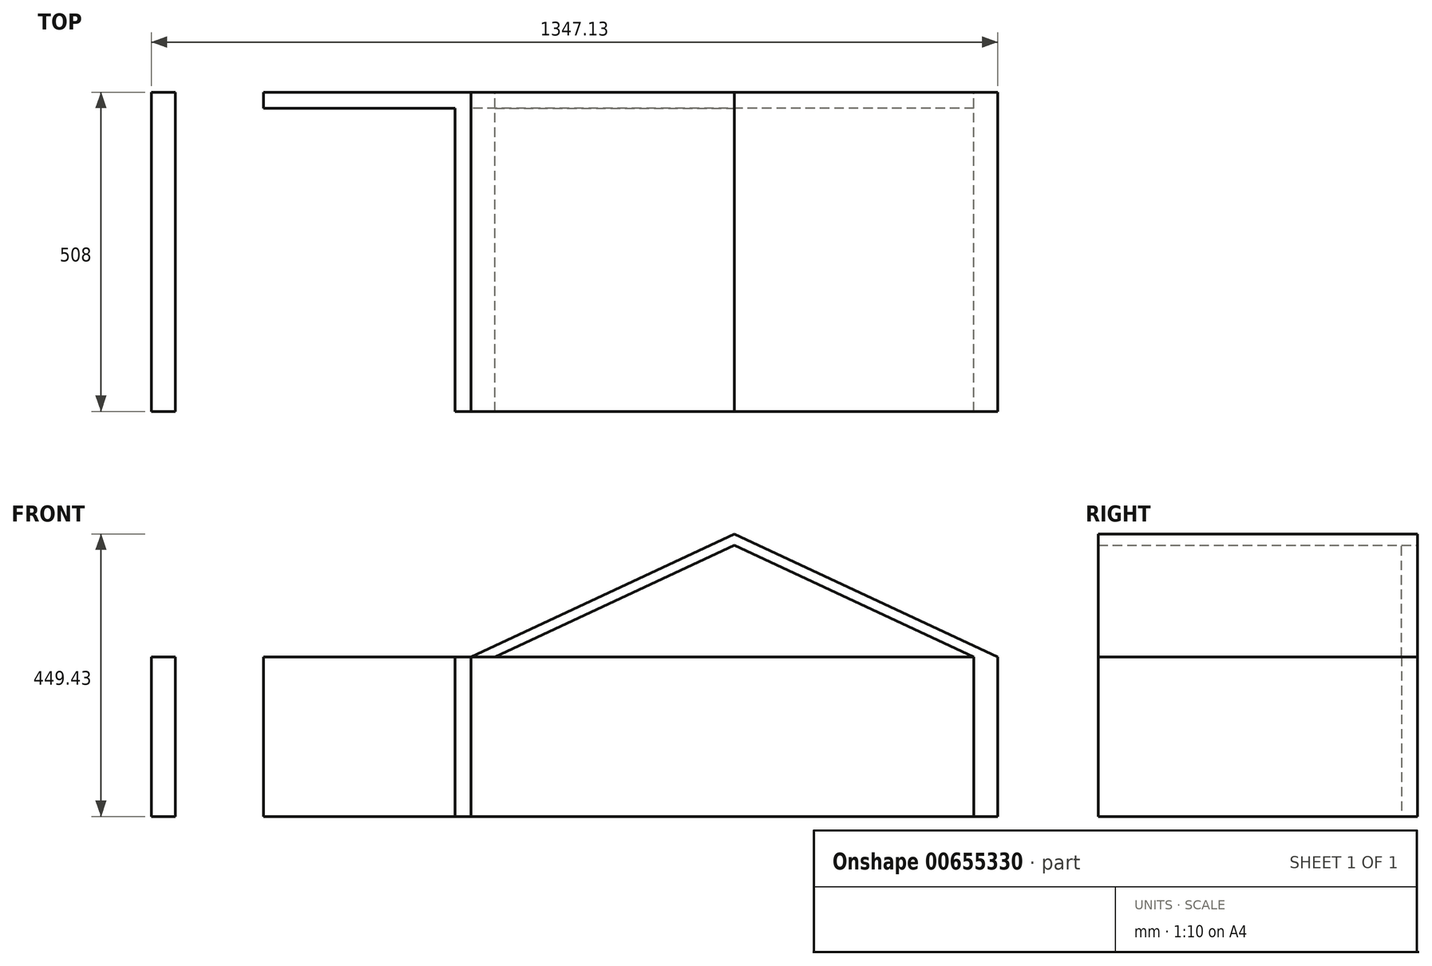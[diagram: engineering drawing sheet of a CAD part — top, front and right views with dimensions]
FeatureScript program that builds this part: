
annotation { "Feature Type Name" : "Feature", "Feature Type Description" : "" }
export const myFeature = defineFeature(function(context is Context, id is Id, definition is map)
    precondition{}
    {
        {
            var Q0;
            Q0=qCreatedBy(makeId("Front.planeOp"),FACE);
            var sketch = newSketch(context, id + "F0", { "sketchPlane" : qUnion([Q0])});
            skLineSegment(sketch, "E0", {"start": v(0, 117.3) * mm, "end": v(0, -136.7) * mm});
            skLineSegment(sketch, "E1", {"start": v(0, -136.7) * mm, "end": v(-25.4, -136.7) * mm});
            skLineSegment(sketch, "E2", {"start": v(-25.4, -136.7) * mm, "end": v(-25.4, 117.3) * mm});
            skLineSegment(sketch, "E3", {"start": v(-25.4, 117.3) * mm, "end": v(0, 117.3) * mm});
            skLineSegment(sketch, "E4", {"start": v(0, -136.7) * mm, "end": v(76.2, -136.7) * mm});
            skLineSegment(sketch, "E5", {"start": v(76.2, -136.7) * mm, "end": v(838.2, -136.7) * mm});
            skLineSegment(sketch, "E6", {"start": v(838.2, -136.7) * mm, "end": v(838.2, 117.3) * mm});
            skLineSegment(sketch, "E7", {"start": v(838.2, 117.3) * mm, "end": v(0, 117.3) * mm});
            skLineSegment(sketch, "E8", {"start": v(0, 117.3) * mm, "end": v(419.1, 312.72) * mm});
            skLineSegment(sketch, "E9", {"start": v(419.1, 312.72) * mm, "end": v(838.2, 117.3) * mm});
            skLineSegment(sketch, "E10", {"start": v(800.1, 117.3) * mm, "end": v(800.1, -136.7) * mm});
            skLineSegment(sketch, "E11", {"start": v(0, 117.3) * mm, "end": v(38.1, 117.3) * mm});
            skLineSegment(sketch, "E12", {"start": v(38.1, 117.3) * mm, "end": v(419.1, 294.95) * mm});
            skLineSegment(sketch, "E13", {"start": v(800.1, 117.3) * mm, "end": v(419.1, 294.95) * mm});
            skLineSegment(sketch, "E14", {"start": v(-470.83, 117.3) * mm, "end": v(-470.83, -136.7) * mm});
            skLineSegment(sketch, "E15", {"start": v(-470.83, 117.3) * mm, "end": v(-508.93, 117.3) * mm});
            skLineSegment(sketch, "E16", {"start": v(-508.93, 117.3) * mm, "end": v(-508.93, -136.7) * mm});
            skLineSegment(sketch, "E17", {"start": v(-508.93, -136.7) * mm, "end": v(-470.83, -136.7) * mm});
            skLineSegment(sketch, "E18", {"start": v(-330.2, 117.3) * mm, "end": v(-330.2, -136.7) * mm});
            skLineSegment(sketch, "E19", {"start": v(-330.2, -136.7) * mm, "end": v(-470.83, -136.7) * mm});
            skLineSegment(sketch, "E20", {"start": v(-330.2, 117.3) * mm, "end": v(-470.83, 117.3) * mm});
            skLineSegment(sketch, "E21", {"start": v(-330.2, 117.3) * mm, "end": v(-25.4, 117.3) * mm});
            skLineSegment(sketch, "E22", {"start": v(-25.4, -136.7) * mm, "end": v(-330.2, -136.7) * mm});
            skSolve(sketch);
        }
        {
            var Q0;
            Q0=makeQuery(id+"F0.imprint","IMPRINT",FACE,{"disambiguationData":[TD([[makeQuery(id+"F0.imprint","IMPRINT",EDGE,{"derivedFrom":sQuery(id+"F0.wireOp",EDGE,"E0")}),-1.0]])]});
            extrude(context, id + "F1", {"entities" : qUnion([Q0]), "depth" : 508 * mm, "offsetDistance" : 25.4 * mm});
        }
        {
            var Q0;
            {var subQ0=sQuery(id+"F0.wireOp",EDGE,"E6");Q0=makeQuery(id+"F0.imprint","IMPRINT",FACE,{"disambiguationData":[TD([[makeQuery(id+"F0.imprint","IMPRINT",EDGE,{"derivedFrom":subQ0}),1.0]])]});}
            extrude(context, id + "F2", {"entities" : qUnion([Q0]), "depth" : 508 * mm, "offsetDistance" : 25.4 * mm});
        }
        {
            var Q0;
            Q0=makeQuery(id+"F0.imprint","IMPRINT",FACE,{"disambiguationData":[TD([[makeQuery(id+"F0.imprint","IMPRINT",EDGE,{"derivedFrom":sQuery(id+"F0.wireOp",EDGE,"E8")}),-1.0]])]});
            extrude(context, id + "F3", {"entities" : qUnion([Q0]), "operationType" : NewBodyOperationType.ADD, "depth" : 508 * mm, "offsetDistance" : 25.4 * mm});
        }
        {
            var Q0;
            Q0=makeQuery(id+"F0.imprint","IMPRINT",FACE,{"disambiguationData":[TD([[makeQuery(id+"F0.imprint","IMPRINT",EDGE,{"derivedFrom":sQuery(id+"F0.wireOp",EDGE,"E0")}),1.0]])]});
            extrude(context, id + "F4", {"entities" : qUnion([Q0]), "depth" : 25.4 * mm, "offsetDistance" : 25.4 * mm});
        }
        {
            var Q0;
            {var subQ0=sQuery(id+"F0.wireOp",EDGE,"E12");Q0=makeQuery(id+"F0.imprint","IMPRINT",FACE,{"disambiguationData":[TD([[makeQuery(id+"F0.imprint","IMPRINT",EDGE,{"derivedFrom":subQ0}),-1.0]])]});}
            extrude(context, id + "F5", {"entities" : qUnion([Q0]), "depth" : 25.4 * mm, "offsetDistance" : 25.4 * mm});
        }
        {
            var Q0;
            Q0=makeQuery(id+"F0.imprint","IMPRINT",FACE,{"disambiguationData":[TD([[makeQuery(id+"F0.imprint","IMPRINT",EDGE,{"derivedFrom":sQuery(id+"F0.wireOp",EDGE,"E2")}),1.0]])]});
            extrude(context, id + "F6", {"entities" : qUnion([Q0]), "operationType" : NewBodyOperationType.ADD, "depth" : 25.4 * mm, "offsetDistance" : 25.4 * mm});
        }
        {
            var Q0;
            Q0=makeQuery(id+"F0.imprint","IMPRINT",FACE,{"disambiguationData":[TD([[makeQuery(id+"F0.imprint","IMPRINT",EDGE,{"derivedFrom":sQuery(id+"F0.wireOp",EDGE,"E14")}),-1.0]])]});
            extrude(context, id + "F7", {"entities" : qUnion([Q0]), "operationType" : NewBodyOperationType.ADD, "depth" : 508 * mm, "offsetDistance" : 25.4 * mm});
        }
    });
